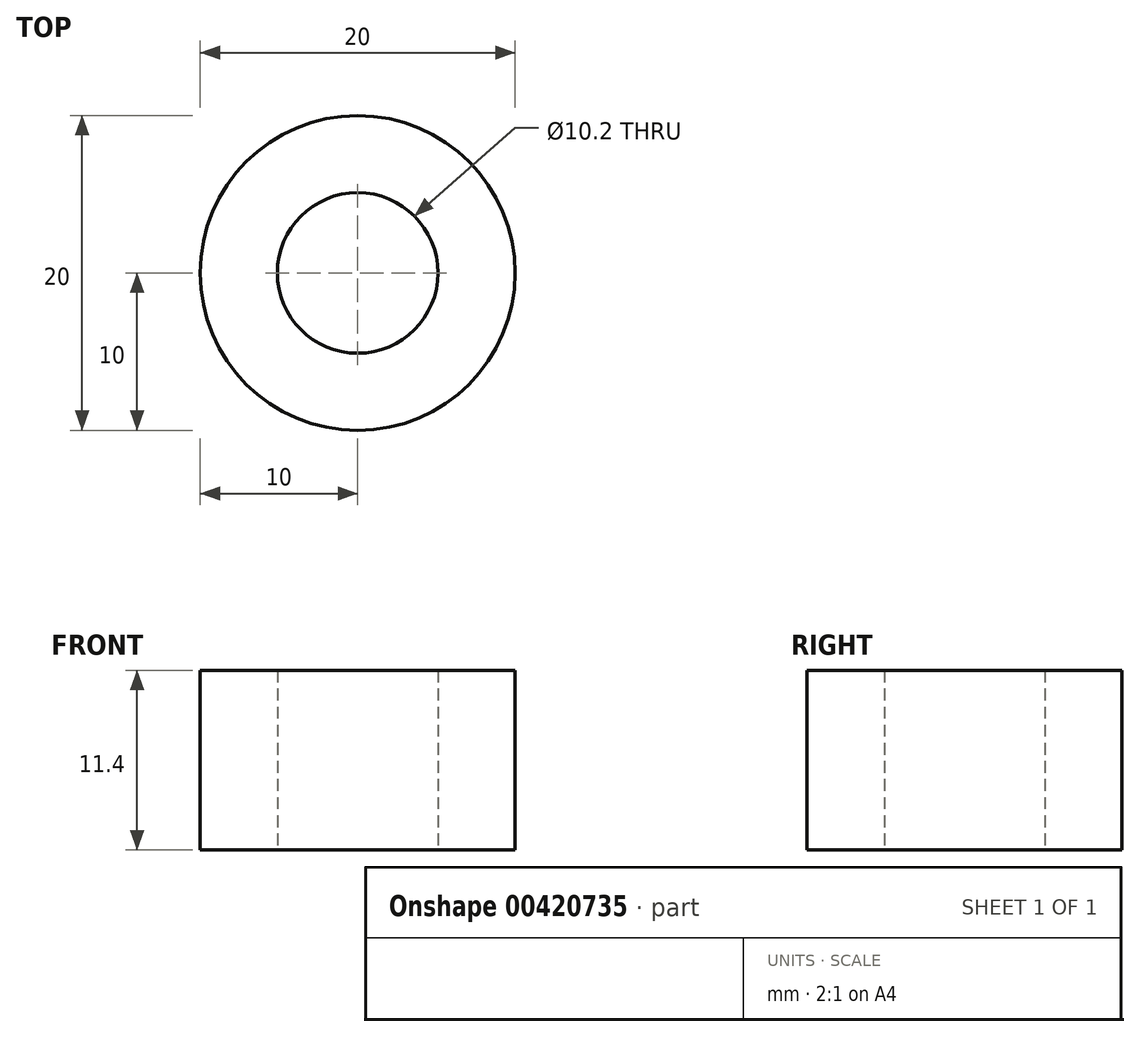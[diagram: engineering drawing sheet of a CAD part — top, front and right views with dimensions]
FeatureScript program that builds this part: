
annotation { "Feature Type Name" : "Feature", "Feature Type Description" : "" }
export const myFeature = defineFeature(function(context is Context, id is Id, definition is map)
    precondition{}
    {
        {
            var Q0;
            Q0=qCreatedBy(makeId("Top.planeOp"),FACE);
            var sketch = newSketch(context, id + "F0", { "sketchPlane" : qUnion([Q0])});
            skCircle(sketch, "E0", {"center": v(0, 0) * mm, "radius": 5.1 * mm});
            skCircle(sketch, "E1", {"center": v(0, 0) * mm, "radius": 10 * mm});
            skSolve(sketch);
        }
        {
            var Q0;
            Q0 = qSketchRegion(id + "F0", true);
            extrude(context, id + "F1", {"entities" : qUnion([Q0]), "depth" : 11.4 * mm});
        }
    });
